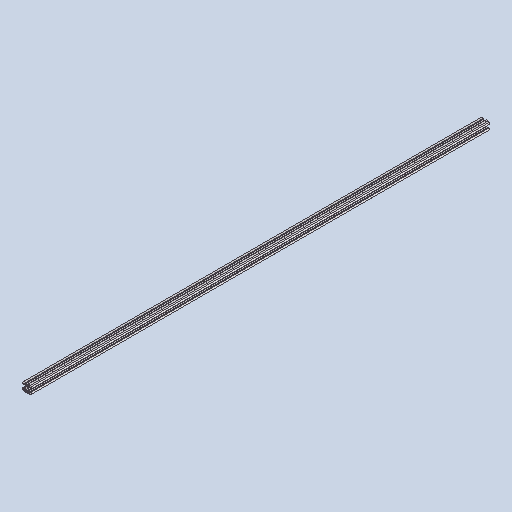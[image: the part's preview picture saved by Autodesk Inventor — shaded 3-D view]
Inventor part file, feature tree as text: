
AUTODESK INVENTOR PART (.ipt)
format: ipt  version: 2025 (Build 290162010, 162A)  size: 243,200 bytes
history: native  units: mm
features: thread x2, chamfer x2, other x1
ambient origin geometry x8: Origin, YZ Plane, XZ Plane, XY Plane, X Axis, Y Axis, Z Axis, Center Point
bodies: Volumenkörper1 (feature_tree)
feature tree (5):
  thread  "Gewinde1"  [1 undecoded]
  thread  "Gewinde2"  [1 undecoded]
  chamfer  "Fasen1"  Distance=2.0mm Angle=45.0deg
  chamfer  "Fasen2"  Distance=2.0mm Angle=45.0deg
  other  "item_43774_profil-5-20x20-1n-natur-_1096_high_1_1:1"
note: 2 required parameter values undecoded (feature->parameter linkage not recoverable at this tier; creation-order binding heuristic only, values carry confidence <= 0.55)
